FCSTD DOCUMENT  (FreeCAD 0.20R29603 (Git))
Label: inqdo
License: All rights reserved
LicenseURL: http://en.wikipedia.org/wiki/All_rights_reserved
objects: Sketcher::SketchObject×5, Image::ImagePlane×1
note: 5 computed .brp shape members not serialized (recipe doc carries the construction recipe); baked Part::Feature solids carry a one-line shape summary decoded from their .brp

FEATURE [Image::ImagePlane] ImagePlane
  XSize = 391.882
  YSize = 139.242
FEATURE [Sketcher::SketchObject] Sketch  label="I"
  FullyConstrained = false
  sketch-geometry (203):
    g0-g101: Circle x102 (B-spline internal-alignment scaffolding for g102; pole/knot coordinates omitted)
    g102: BSplineCurve PolesCount=102 KnotsCount=100 Degree=3 IsPeriodic=0
    g103-g202: GeomPoint x100 (B-spline internal-alignment scaffolding for g102; pole/knot coordinates omitted)
  constraints (26):
    c: Weight(g0) = 1
    c: Equal(g0, g1-g7) x7
    c: PointOnObject(g7,g6)
    c: Equal(g0, g8-g11) x4
    c: PointOnObject(g11,g10)
    c: Equal(g0,g12)
    c: PointOnObject(g12,g11)
    c: Equal(g0, g13-g38) x26
    c: PointOnObject(g38,g37)
    c: Equal(g0, g39-g46) x8
    c: PointOnObject(g46,g45)
    c: Equal(g0,g47)
    c: PointOnObject(g47,g46)
    c: Equal(g0, g48-g60) x13
    c: PointOnObject(g60,g59)
    c: Equal(g0, g61-g69) x9
    c: PointOnObject(g69,g68)
    c: Equal(g0,g70)
    c: Equal(g0,g71)
    c: PointOnObject(g71,g70)
    c: Equal(g0, g72-g95) x24
    c: PointOnObject(g95,g94)
    c: Equal(g0, g96-g101) x6
    c: Coincident(g102,g0)
    c: InternalAlignment(g0-g101 -> g102) x102
    c: InternalAlignment(g103-g202 -> g102) x100
FEATURE [Sketcher::SketchObject] Sketch001  label="N"
  FullyConstrained = false
  sketch-geometry (239):
    g0-g119: Circle x120 (B-spline internal-alignment scaffolding for g120; pole/knot coordinates omitted)
    g120: BSplineCurve PolesCount=120 KnotsCount=118 Degree=3 IsPeriodic=0
    g121-g238: GeomPoint x118 (B-spline internal-alignment scaffolding for g120; pole/knot coordinates omitted)
  constraints (50):
    c: Weight(g0) = 1
    c: Equal(g0,g1)
    c: PointOnObject(g1,g0)
    c: Equal(g0,g2)
    c: PointOnObject(g2,g1)
    c: Equal(g0,g3)
    c: PointOnObject(g3,g2)
    c: Equal(g0,g4)
    c: PointOnObject(g4,g3)
    c: Equal(g0,g5)
    c: Equal(g0,g6)
    c: PointOnObject(g6,g5)
    c: Equal(g0, g7-g10) x4
    c: PointOnObject(g10,g-1)
    c: Equal(g0, g11-g28) x18
    c: PointOnObject(g28,g27)
    c: Equal(g0,g29)
    c: Equal(g0,g30)
    c: PointOnObject(g30,g29)
    c: Equal(g0,g31)
    c: Equal(g0,g32)
    c: PointOnObject(g32,g31)
    c: Equal(g0,g33)
    c: PointOnObject(g33,g32)
    c: Equal(g0, g34-g48) x15
    c: PointOnObject(g48,g47)
    c: Equal(g0,g49)
    c: Equal(g0,g50)
    c: Equal(g0,g51)
    c: PointOnObject(g51,g49)
    c: Equal(g0,g52)
    c: PointOnObject(g52,g51)
    c: Equal(g0,g53)
    c: Equal(g0,g54)
    c: PointOnObject(g54,g53)
    c: Equal(g0, g55-g93) x39
    c: PointOnObject(g93,g92)
    c: Equal(g0,g94)
    c: PointOnObject(g94,g92)
    c: Equal(g0,g95)
    c: PointOnObject(g95,g92)
    c: Equal(g0, g96-g102) x7
    c: PointOnObject(g102,g101)
    c: Equal(g0, g103-g117) x15
    c: PointOnObject(g117,g116)
    c: Equal(g0,g118)
    c: Equal(g0,g119)
    c: Coincident(g120,g0)
    c: InternalAlignment(g0-g119 -> g120) x120
    c: InternalAlignment(g121-g238 -> g120) x118
FEATURE [Sketcher::SketchObject] Sketch002  label="Q"
  FullyConstrained = false
  MapMode = 2
  Support = -> [ImagePlane]
  sketch-geometry (471):
    g0-g235: Circle x236 (B-spline internal-alignment scaffolding for g236; pole/knot coordinates omitted)
    g236: BSplineCurve PolesCount=236 KnotsCount=234 Degree=3 IsPeriodic=0
    g237-g470: GeomPoint x234 (B-spline internal-alignment scaffolding for g236; pole/knot coordinates omitted)
  constraints (41):
    c: Weight(g0) = 1
    c: Equal(g0,g1)
    c: Equal(g0,g2)
    c: Equal(g0,g3)
    c: PointOnObject(g3,g1)
    c: Equal(g0, g4-g44) x41
    c: PointOnObject(g44,g-2)
    c: Equal(g0,g45)
    c: Equal(g0,g46)
    c: PointOnObject(g46,g45)
    c: Equal(g0, g47-g63) x17
    c: PointOnObject(g63,g61)
    c: Equal(g0,g64)
    c: PointOnObject(g64,g63)
    c: Equal(g0,g65)
    c: PointOnObject(g65,g64)
    c: Equal(g0, g66-g71) x6
    c: PointOnObject(g71,g70)
    c: Equal(g0,g72)
    c: Equal(g0,g73)
    c: Equal(g0,g74)
    c: PointOnObject(g74,g73)
    c: Equal(g0, g75-g85) x11
    c: PointOnObject(g85,g83)
    c: Equal(g0, g86-g124) x39
    c: PointOnObject(g124,g123)
    c: Equal(g0, g125-g170) x46
    c: PointOnObject(g170,g168)
    c: Equal(g0,g171)
    c: PointOnObject(g171,g170)
    c: Equal(g0, g172-g182) x11
    c: PointOnObject(g182,g181)
    c: Equal(g0,g183)
    c: Equal(g0,g184)
    c: PointOnObject(g184,g182)
    c: Equal(g0, g185-g230) x46
    c: PointOnObject(g230,g229)
    c: Equal(g0, g231-g235) x5
    c: Coincident(g236,g0)
    c: InternalAlignment(g0-g235 -> g236) x236
    c: InternalAlignment(g237-g470 -> g236) x234
FEATURE [Sketcher::SketchObject] Sketch003  label="D"
  FullyConstrained = false
  MapMode = 2
  Support = -> [ImagePlane]
  sketch-geometry (267):
    g0-g133: Circle x134 (B-spline internal-alignment scaffolding for g134; pole/knot coordinates omitted)
    g134: BSplineCurve PolesCount=134 KnotsCount=132 Degree=3 IsPeriodic=0
    g135-g266: GeomPoint x132 (B-spline internal-alignment scaffolding for g134; pole/knot coordinates omitted)
  constraints (22):
    c: Weight(g0) = 1
    c: Equal(g0,g1)
    c: PointOnObject(g1,g0)
    c: Equal(g0, g2-g122) x121
    c: PointOnObject(g122,g121)
    c: Equal(g0,g123)
    c: Equal(g0,g124)
    c: Equal(g0,g125)
    c: PointOnObject(g125,g124)
    c: Equal(g0,g126)
    c: Equal(g0,g127)
    c: Equal(g0,g128)
    c: PointOnObject(g128,g127)
    c: Equal(g0,g129)
    c: Equal(g0,g130)
    c: Equal(g0,g131)
    c: PointOnObject(g131,g129)
    c: Equal(g0,g132)
    c: Equal(g0,g133)
    c: Coincident(g134,g0)
    c: InternalAlignment(g0-g133 -> g134) x134
    c: InternalAlignment(g135-g266 -> g134) x132
FEATURE [Sketcher::SketchObject] Sketch004  label="O"
  FullyConstrained = false
  MapMode = 2
  Support = -> [Sketch003]
  sketch-geometry (239):
    g0-g119: Circle x120 (B-spline internal-alignment scaffolding for g120; pole/knot coordinates omitted)
    g120: BSplineCurve PolesCount=120 KnotsCount=118 Degree=3 IsPeriodic=0
    g121-g238: GeomPoint x118 (B-spline internal-alignment scaffolding for g120; pole/knot coordinates omitted)
  constraints (9):
    c: Weight(g0) = 1
    c: Equal(g0, g1-g117) x117
    c: PointOnObject(g117,g0)
    c: Equal(g0,g118)
    c: PointOnObject(g118,g117)
    c: Equal(g0,g119)
    c: Coincident(g120,g1)
    c: InternalAlignment(g0-g119 -> g120) x120
    c: InternalAlignment(g121-g238 -> g120) x118
